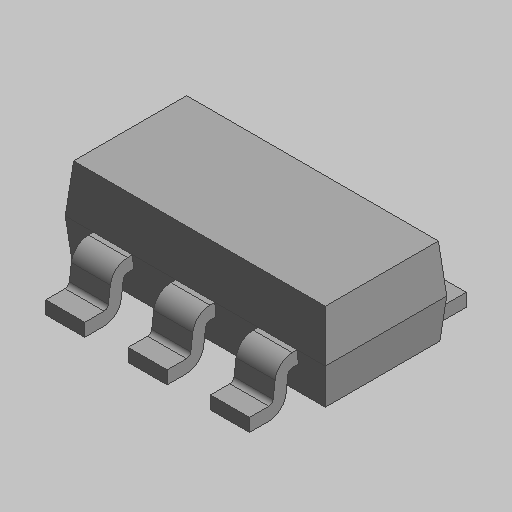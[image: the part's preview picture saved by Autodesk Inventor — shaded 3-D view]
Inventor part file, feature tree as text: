
AUTODESK INVENTOR PART (.ipt)
format: ipt  version: 2023.5 (Build 275446000, 446)  size: 108,032 bytes
history: native  units: mm (DEFAULTED — no unit token found)
features: fillet x1
ambient origin geometry x8: Origin, YZ Plane, XZ Plane, XY Plane, X Axis, Y Axis, Z Axis, Center Point
bodies: Solid1 (feature_tree)
feature tree (1):
  fillet  "Fillet2"  [1 undecoded]
note: 1 required parameter value undecoded (feature->parameter linkage not recoverable at this tier; creation-order binding heuristic only, values carry confidence <= 0.55)
